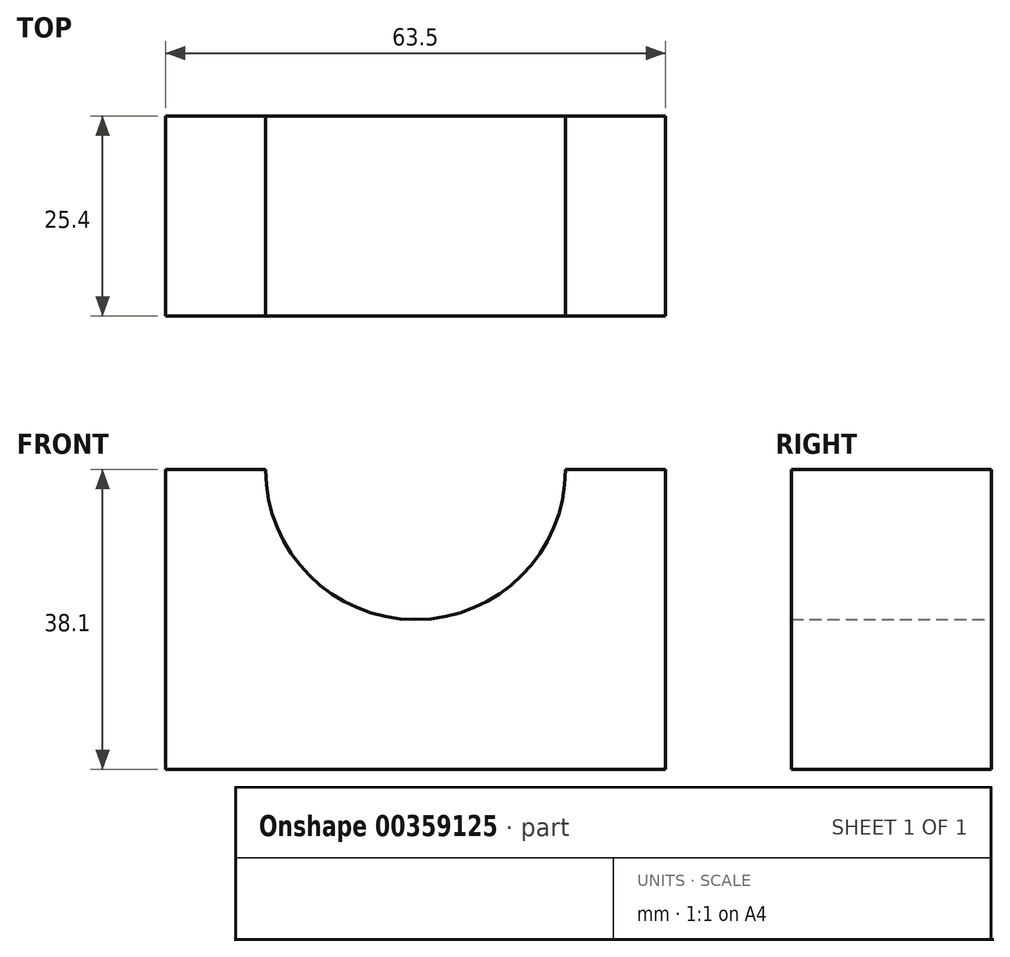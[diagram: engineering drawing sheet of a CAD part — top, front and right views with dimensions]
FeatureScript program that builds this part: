
annotation { "Feature Type Name" : "Feature", "Feature Type Description" : "" }
export const myFeature = defineFeature(function(context is Context, id is Id, definition is map)
    precondition{}
    {
        {
            var Q0;
            Q0=qCreatedBy(makeId("Front.planeOp"),FACE);
            var sketch = newSketch(context, id + "F0", { "sketchPlane" : qUnion([Q0])});
            skLineSegment(sketch, "E0", {"start": v(0, 0) * mm, "end": v(63.5, 0) * mm});
            skLineSegment(sketch, "E1", {"start": v(63.5, 0) * mm, "end": v(63.5, 38.1) * mm});
            skLineSegment(sketch, "E2", {"start": v(63.5, 38.1) * mm, "end": v(0, 38.1) * mm});
            skLineSegment(sketch, "E3", {"start": v(0, 38.1) * mm, "end": v(0, 0) * mm});
            skArc(sketch, "E4", {"start": v(12.7, 38.1) * mm, "mid": v(31.75, 19.05) * mm, "end": v(50.8, 38.1) * mm});
            skSolve(sketch);
        }
        {
            var Q0;
            Q0=makeQuery(id+"F0.imprint","IMPRINT",FACE,{"disambiguationData":[TD([[makeQuery(id+"F0.imprint","IMPRINT",EDGE,{"derivedFrom":sQuery(id+"F0.wireOp",EDGE,"E0")}),1.0]])]});
            extrude(context, id + "F1", {"entities" : qUnion([Q0]), "depth" : 25.4 * mm});
        }
    });
